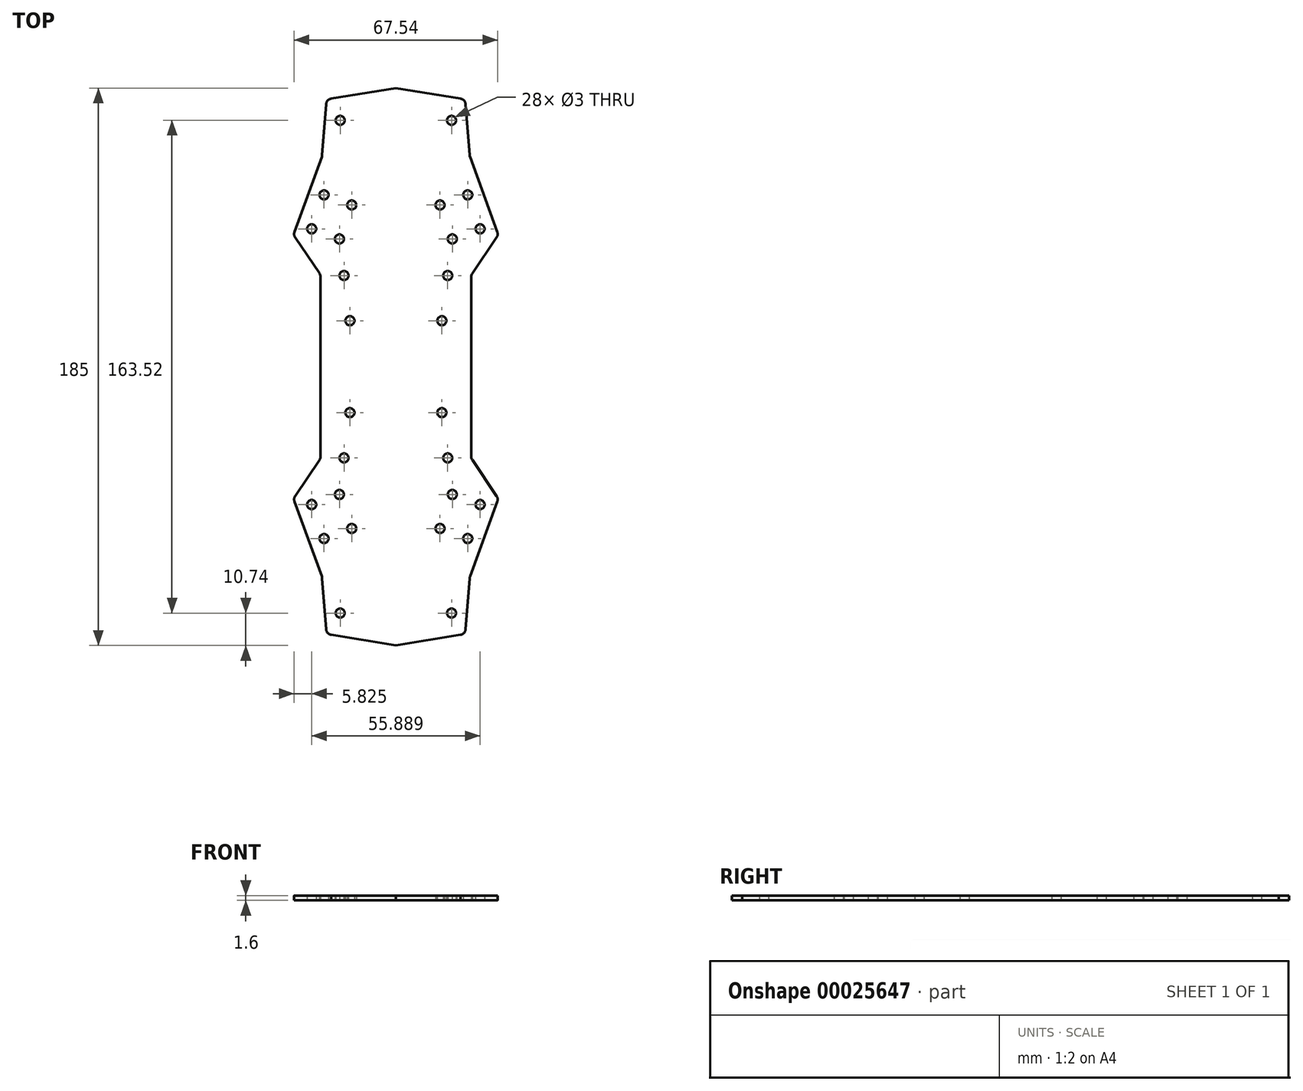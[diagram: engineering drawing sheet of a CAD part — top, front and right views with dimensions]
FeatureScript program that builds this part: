
annotation { "Feature Type Name" : "Feature", "Feature Type Description" : "" }
export const myFeature = defineFeature(function(context is Context, id is Id, definition is map)
    precondition{}
    {
        {
            var Q0;
            Q0=qCreatedBy(makeId("Top.planeOp"),FACE);
            var sketch = newSketch(context, id + "F0", { "sketchPlane" : qUnion([Q0])});
            skLineSegment(sketch, "E0.0", {"start": v(-33.43, 42.92) * mm, "end": v(-25.34, 30.92) * mm});
            skLineSegment(sketch, "E1.0", {"start": v(-24.57, 69.66) * mm, "end": v(-33.65, 44.72) * mm});
            skLineSegment(sketch, "E2.0", {"start": v(-23.12, 87.16) * mm, "end": v(-24.46, 70.2) * mm});
            skArc(sketch, "E3.0", {"start": v(-33.65, 44.72) * mm, "mid": v(-33.76, 43.79) * mm, "end": v(-33.43, 42.92) * mm});
            skCircle(sketch, "E4.0", {"center": v(-27.94, 45.74) * mm, "radius": 1.5 * mm});
            skCircle(sketch, "E5.0", {"center": v(-18.73, 42.4) * mm, "radius": 1.5 * mm});
            skCircle(sketch, "E5.1", {"center": v(-17.2, 30.26) * mm, "radius": 1.5 * mm});
            skArc(sketch, "E6.0", {"start": v(-21.47, 88.97) * mm, "mid": v(-22.6, 88.35) * mm, "end": v(-23.12, 87.16) * mm});
            skCircle(sketch, "E7.0", {"center": v(-18.47, 81.76) * mm, "radius": 1.5 * mm});
            skCircle(sketch, "E8.0", {"center": v(-23.85, 57.02) * mm, "radius": 1.5 * mm});
            skCircle(sketch, "E9.0", {"center": v(-14.64, 53.68) * mm, "radius": 1.5 * mm});
            skArc(sketch, "E10.0", {"start": v(-24.46, 70.2) * mm, "mid": v(-24.5, 69.92) * mm, "end": v(-24.57, 69.66) * mm});
            skCircle(sketch, "E11.0", {"center": v(-15.25, 15.25) * mm, "radius": 1.5 * mm});
            skArc(sketch, "E12.0", {"start": v(-25.34, 30.92) * mm, "mid": v(-25.09, 30.4) * mm, "end": v(-25, 29.8) * mm});
            skLineSegment(sketch, "E13", {"start": v(0, 0) * mm, "end": v(0, 92.5) * mm, "construction": true});
            skLineSegment(sketch, "E14", {"start": v(0, 0) * mm, "end": v(0, -92.5) * mm, "construction": true});
            skCircle(sketch, "E15.2.MirrorC", {"center": v(15.25, 15.25) * mm, "radius": 1.5 * mm});
            skCircle(sketch, "E15.3.MirrorC", {"center": v(17.2, 30.26) * mm, "radius": 1.5 * mm});
            skCircle(sketch, "E16.0.MirrorC", {"center": v(-15.25, -15.25) * mm, "radius": 1.5 * mm});
            skCircle(sketch, "E17.0.MirrorC", {"center": v(15.25, -15.25) * mm, "radius": 1.5 * mm});
            skLineSegment(sketch, "E18", {"start": v(-25, 0) * mm, "end": v(25, 0) * mm});
            skLineSegment(sketch, "E19", {"start": v(-25, 0) * mm, "end": v(-25, 29.8) * mm});
            skArc(sketch, "E20.0.MirrorCS", {"start": v(-24.46, -70.2) * mm, "mid": v(-24.5, -69.92) * mm, "end": v(-24.57, -69.66) * mm});
            skCircle(sketch, "E20.1.MirrorC", {"center": v(-18.73, -42.4) * mm, "radius": 1.5 * mm});
            skArc(sketch, "E20.2.MirrorCS", {"start": v(-25.34, -30.92) * mm, "mid": v(-25.09, -30.4) * mm, "end": v(-25, -29.8) * mm});
            skCircle(sketch, "E20.3.MirrorC", {"center": v(-23.85, -57.02) * mm, "radius": 1.5 * mm});
            skLineSegment(sketch, "E20.4.MirrorCS", {"start": v(-33.43, -42.92) * mm, "end": v(-25.34, -30.92) * mm});
            skCircle(sketch, "E20.5.MirrorC", {"center": v(-18.47, -81.76) * mm, "radius": 1.5 * mm});
            skCircle(sketch, "E20.6.MirrorC", {"center": v(-27.94, -45.74) * mm, "radius": 1.5 * mm});
            skLineSegment(sketch, "E20.8.MirrorCS", {"start": v(-23.12, -87.16) * mm, "end": v(-24.46, -70.2) * mm});
            skCircle(sketch, "E20.9.MirrorC", {"center": v(-14.64, -53.68) * mm, "radius": 1.5 * mm});
            skArc(sketch, "E20.10.MirrorCS", {"start": v(-33.65, -44.72) * mm, "mid": v(-33.76, -43.79) * mm, "end": v(-33.43, -42.92) * mm});
            skLineSegment(sketch, "E20.11.MirrorCS", {"start": v(-25, 0) * mm, "end": v(-25, -29.8) * mm});
            skCircle(sketch, "E20.12.MirrorC", {"center": v(-17.2, -30.26) * mm, "radius": 1.5 * mm});
            skArc(sketch, "E20.13.MirrorCS", {"start": v(-21.47, -88.97) * mm, "mid": v(-22.6, -88.35) * mm, "end": v(-23.12, -87.16) * mm});
            skLineSegment(sketch, "E20.14.MirrorCS", {"start": v(-24.57, -69.66) * mm, "end": v(-33.65, -44.72) * mm});
            skArc(sketch, "E21.0.MirrorCS", {"start": v(24.46, 70.2) * mm, "mid": v(24.5, 69.92) * mm, "end": v(24.57, 69.66) * mm});
            skLineSegment(sketch, "E21.1.MirrorCS", {"start": v(23.12, 87.16) * mm, "end": v(24.46, 70.2) * mm});
            skArc(sketch, "E21.2.MirrorCS", {"start": v(25.34, 30.92) * mm, "mid": v(25.09, 30.4) * mm, "end": v(25, 29.8) * mm});
            skArc(sketch, "E21.3.MirrorCS", {"start": v(33.65, 44.72) * mm, "mid": v(33.76, 43.79) * mm, "end": v(33.43, 42.92) * mm});
            skCircle(sketch, "E21.4.MirrorC", {"center": v(23.85, 57.02) * mm, "radius": 1.5 * mm});
            skCircle(sketch, "E21.5.MirrorC", {"center": v(27.94, 45.74) * mm, "radius": 1.5 * mm});
            skLineSegment(sketch, "E21.6.MirrorCS", {"start": v(33.43, 42.92) * mm, "end": v(25.34, 30.92) * mm});
            skLineSegment(sketch, "E21.7.MirrorCS", {"start": v(24.57, 69.66) * mm, "end": v(33.65, 44.72) * mm});
            skArc(sketch, "E21.8.MirrorCS", {"start": v(21.47, 88.97) * mm, "mid": v(22.6, 88.35) * mm, "end": v(23.12, 87.16) * mm});
            skLineSegment(sketch, "E22.0.MirrorCS", {"start": v(25, 0) * mm, "end": v(25, 29.8) * mm});
            skCircle(sketch, "E23.0.MirrorC", {"center": v(18.73, 42.4) * mm, "radius": 1.5 * mm});
            skCircle(sketch, "E24.0.MirrorC", {"center": v(14.64, 53.68) * mm, "radius": 1.5 * mm});
            skArc(sketch, "E25.0.MirrorCS", {"start": v(21.47, -88.97) * mm, "mid": v(22.6, -88.35) * mm, "end": v(23.12, -87.16) * mm});
            skCircle(sketch, "E25.1.MirrorC", {"center": v(27.94, -45.74) * mm, "radius": 1.5 * mm});
            skArc(sketch, "E25.2.MirrorCS", {"start": v(33.65, -44.72) * mm, "mid": v(33.76, -43.79) * mm, "end": v(33.43, -42.92) * mm});
            skArc(sketch, "E25.3.MirrorCS", {"start": v(25.34, -30.92) * mm, "mid": v(25.09, -30.4) * mm, "end": v(25, -29.8) * mm});
            skLineSegment(sketch, "E25.4.MirrorCS", {"start": v(24.57, -69.66) * mm, "end": v(33.65, -44.72) * mm});
            skLineSegment(sketch, "E25.5.MirrorCS", {"start": v(23.12, -87.16) * mm, "end": v(24.46, -70.2) * mm});
            skArc(sketch, "E25.6.MirrorCS", {"start": v(24.46, -70.2) * mm, "mid": v(24.5, -69.92) * mm, "end": v(24.57, -69.66) * mm});
            skLineSegment(sketch, "E25.7.MirrorCS", {"start": v(33.43, -42.92) * mm, "end": v(25.34, -30.92) * mm});
            skCircle(sketch, "E25.8.MirrorC", {"center": v(23.85, -57.02) * mm, "radius": 1.5 * mm});
            skLineSegment(sketch, "E26.0.MirrorCS", {"start": v(25, 0) * mm, "end": v(25, -29.8) * mm});
            skCircle(sketch, "E27.0.MirrorC", {"center": v(18.73, -42.4) * mm, "radius": 1.5 * mm});
            skCircle(sketch, "E28.0.MirrorC", {"center": v(14.64, -53.68) * mm, "radius": 1.5 * mm});
            skCircle(sketch, "E29.0.MirrorC", {"center": v(18.47, -81.76) * mm, "radius": 1.5 * mm});
            skCircle(sketch, "E30.0.MirrorC", {"center": v(17.2, -30.26) * mm, "radius": 1.5 * mm});
            skLineSegment(sketch, "E31", {"start": v(-21.47, 88.97) * mm, "end": v(0, 92.5) * mm});
            skLineSegment(sketch, "E32", {"start": v(21.47, 88.97) * mm, "end": v(0, 92.5) * mm});
            skLineSegment(sketch, "E33", {"start": v(0, -92.5) * mm, "end": v(-21.47, -88.97) * mm});
            skLineSegment(sketch, "E34", {"start": v(0, -92.5) * mm, "end": v(21.47, -88.97) * mm});
            skLineSegment(sketch, "E35", {"start": v(-23.85, 57.02) * mm, "end": v(-14.64, 53.68) * mm, "construction": true});
            skLineSegment(sketch, "E36", {"start": v(-14.64, 53.68) * mm, "end": v(-18.73, 42.4) * mm, "construction": true});
            skLineSegment(sketch, "E37", {"start": v(-18.73, 42.4) * mm, "end": v(-27.94, 45.74) * mm, "construction": true});
            skLineSegment(sketch, "E38", {"start": v(-27.94, 45.74) * mm, "end": v(-23.85, 57.02) * mm, "construction": true});
            skCircle(sketch, "E39.0.MirrorC", {"center": v(18.47, 81.76) * mm, "radius": 1.5 * mm});
            skSolve(sketch);
        }
        {
            var Q0;
            Q0=qSketchRegion(id+"F0",true);
            extrude(context, id + "F1", {"entities" : qUnion([Q0]), "depth" : 1.6 * mm});
        }
    });
